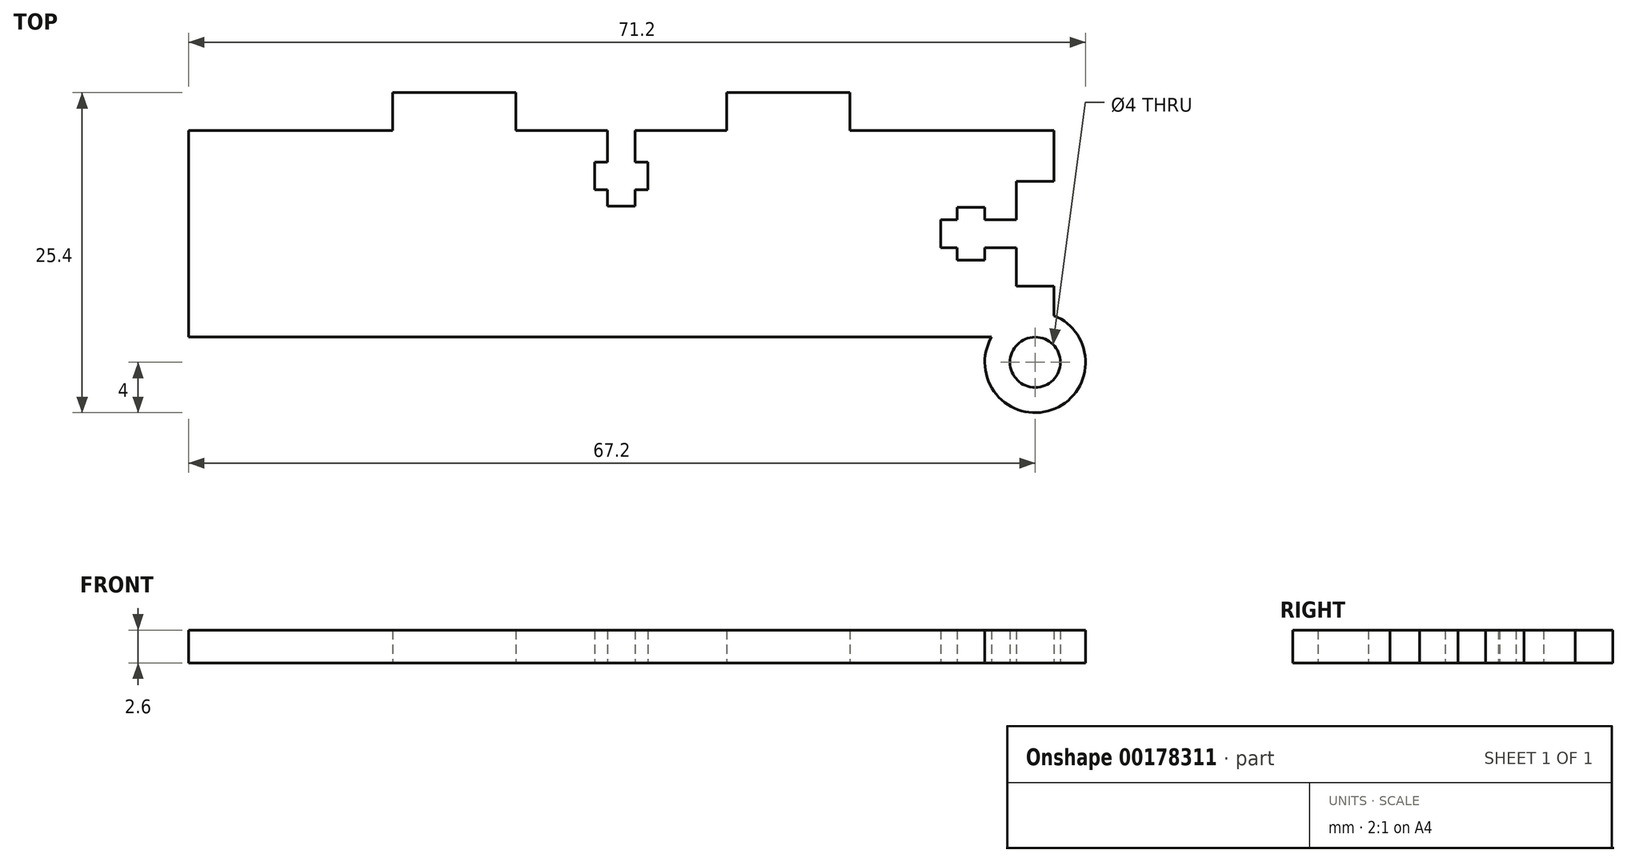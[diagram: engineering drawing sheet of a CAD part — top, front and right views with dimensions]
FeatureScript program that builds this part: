
annotation { "Feature Type Name" : "Feature", "Feature Type Description" : "" }
export const myFeature = defineFeature(function(context is Context, id is Id, definition is map)
    precondition{}
    {
        {
            var Q0;
            Q0=qCreatedBy(makeId("Top.planeOp"),FACE);
            var sketch = newSketch(context, id + "F0", { "sketchPlane" : qUnion([Q0])});
            skLineSegment(sketch, "E0.bottom", {"start": v(34.35, 8.2) * mm, "end": v(18.15, 8.2) * mm});
            skLineSegment(sketch, "E0.left", {"start": v(34.35, 8.2) * mm, "end": v(34.35, 4.15) * mm});
            skLineSegment(sketch, "E0.right", {"start": v(-34.35, 8.2) * mm, "end": v(-34.35, -8.2) * mm});
            skPoint(sketch, "E0.middle", {"position": v(0, 0) * mm});
            skLineSegment(sketch, "E1.top", {"start": v(-18.15, 11.2) * mm, "end": v(-8.35, 11.2) * mm});
            skLineSegment(sketch, "E1.left", {"start": v(-18.15, 8.2) * mm, "end": v(-18.15, 11.2) * mm});
            skLineSegment(sketch, "E1.right", {"start": v(-8.35, 8.2) * mm, "end": v(-8.35, 11.2) * mm});
            skLineSegment(sketch, "E2.top", {"start": v(8.35, 11.2) * mm, "end": v(18.15, 11.2) * mm});
            skLineSegment(sketch, "E2.left", {"start": v(8.35, 8.2) * mm, "end": v(8.35, 11.2) * mm});
            skLineSegment(sketch, "E2.right", {"start": v(18.15, 8.2) * mm, "end": v(18.15, 11.2) * mm});
            skLineSegment(sketch, "E3.bottom", {"start": v(34.35, -4.15) * mm, "end": v(31.35, -4.15) * mm});
            skLineSegment(sketch, "E3.top", {"start": v(34.35, 4.15) * mm, "end": v(31.35, 4.15) * mm});
            skLineSegment(sketch, "E3.right", {"start": v(31.35, -4.15) * mm, "end": v(31.35, -1.1) * mm});
            skLineSegment(sketch, "E4", {"start": v(32.85, -4.15) * mm, "end": v(32.85, -23.58) * mm, "construction": true});
            skArc(sketch, "E5", {"start": v(29.39, -8.2) * mm, "mid": v(34.15, -13.98) * mm, "end": v(34.35, -6.5) * mm});
            skLineSegment(sketch, "E6.top", {"start": v(-1.1, 2.2) * mm, "end": v(1.1, 2.2) * mm});
            skLineSegment(sketch, "E6.left", {"start": v(-1.1, 8.2) * mm, "end": v(-1.1, 5.7) * mm});
            skLineSegment(sketch, "E6.right", {"start": v(1.1, 8.2) * mm, "end": v(1.1, 5.7) * mm});
            skLineSegment(sketch, "E7.bottom", {"start": v(2.1, 5.7) * mm, "end": v(1.1, 5.7) * mm});
            skLineSegment(sketch, "E7.top", {"start": v(2.1, 3.5) * mm, "end": v(1.1, 3.5) * mm});
            skLineSegment(sketch, "E7.left", {"start": v(2.1, 5.7) * mm, "end": v(2.1, 3.5) * mm});
            skLineSegment(sketch, "E7.right", {"start": v(-2.1, 5.7) * mm, "end": v(-2.1, 3.5) * mm});
            skPoint(sketch, "E7.middle", {"position": v(0, 4.6) * mm});
            skPoint(sketch, "E8.middle", {"position": v(22.46, 0) * mm});
            skLineSegment(sketch, "E9.top", {"start": v(25.35, 1.1) * mm, "end": v(25.35, -1.1) * mm});
            skLineSegment(sketch, "E9.left", {"start": v(31.35, 1.1) * mm, "end": v(28.85, 1.1) * mm});
            skLineSegment(sketch, "E9.right", {"start": v(31.35, -1.1) * mm, "end": v(28.85, -1.1) * mm});
            skLineSegment(sketch, "E10.bottom", {"start": v(28.85, -2.1) * mm, "end": v(28.85, -1.1) * mm});
            skLineSegment(sketch, "E10.top", {"start": v(26.65, -2.1) * mm, "end": v(26.65, -1.1) * mm});
            skLineSegment(sketch, "E10.left", {"start": v(28.85, -2.1) * mm, "end": v(26.65, -2.1) * mm});
            skLineSegment(sketch, "E10.right", {"start": v(28.85, 2.1) * mm, "end": v(26.65, 2.1) * mm});
            skPoint(sketch, "E10.middle", {"position": v(27.75, 0) * mm});
            skLineSegment(sketch, "E11.trimOffspring", {"start": v(-18.15, 8.2) * mm, "end": v(-34.35, 8.2) * mm});
            skLineSegment(sketch, "E12.trimOffspring", {"start": v(8.35, 8.2) * mm, "end": v(1.1, 8.2) * mm});
            skLineSegment(sketch, "E13.trimOffspring", {"start": v(-1.1, 5.7) * mm, "end": v(-2.1, 5.7) * mm});
            skLineSegment(sketch, "E14.trimOffspring", {"start": v(1.1, 3.5) * mm, "end": v(1.1, 2.2) * mm});
            skLineSegment(sketch, "E15.trimOffspring", {"start": v(-1.1, 3.5) * mm, "end": v(-1.1, 2.2) * mm});
            skLineSegment(sketch, "E16.trimOffspring", {"start": v(-1.1, 3.5) * mm, "end": v(-2.1, 3.5) * mm});
            skLineSegment(sketch, "E17.trimOffspring", {"start": v(26.65, 1.1) * mm, "end": v(26.65, 2.1) * mm});
            skLineSegment(sketch, "E18.trimOffspring", {"start": v(28.85, 1.1) * mm, "end": v(28.85, 2.1) * mm});
            skLineSegment(sketch, "E19.trimOffspring", {"start": v(26.65, 1.1) * mm, "end": v(25.35, 1.1) * mm});
            skLineSegment(sketch, "E20.trimOffspring", {"start": v(26.65, -1.1) * mm, "end": v(25.35, -1.1) * mm});
            skLineSegment(sketch, "E21.trimOffspring", {"start": v(29.39, -8.2) * mm, "end": v(-34.35, -8.2) * mm});
            skPoint(sketch, "E0.top.start.orphan", {"position": v(34.35, -8.2) * mm});
            skLineSegment(sketch, "E22.trimOffspring", {"start": v(31.35, 1.1) * mm, "end": v(31.35, 4.15) * mm});
            skLineSegment(sketch, "E23.trimOffspring", {"start": v(34.35, -4.15) * mm, "end": v(34.35, -6.5) * mm});
            skLineSegment(sketch, "E24.trimOffspring", {"start": v(-1.1, 8.2) * mm, "end": v(-8.35, 8.2) * mm});
            skCircle(sketch, "E25", {"center": v(32.85, -10.2) * mm, "radius": 2 * mm});
            skSolve(sketch);
        }
        {
            var Q0;
            Q0=makeQuery(id+"F0.imprint","IMPRINT",FACE,{"disambiguationData":[TD([[makeQuery(id+"F0.imprint","IMPRINT",EDGE,{"derivedFrom":sQuery(id+"F0.wireOp",EDGE,"E0.bottom")}),1.0]])]});
            extrude(context, id + "F1", {"entities" : qUnion([Q0]), "depth" : 2.6 * mm});
        }
    });
